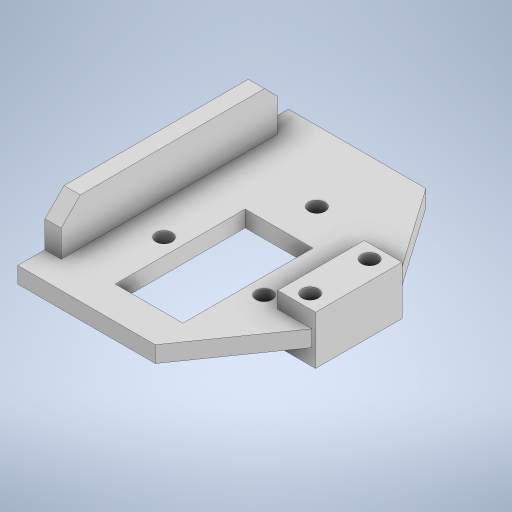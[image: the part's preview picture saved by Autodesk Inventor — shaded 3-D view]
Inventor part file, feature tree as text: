
AUTODESK INVENTOR PART (.ipt)
format: ipt  version: 2023 (Build 270158000, 158)  size: 316,416 bytes
history: native  units: mm
features: extrude x4, sketch x4, other x1
ambient origin geometry x8: Origin, YZ Plane, XZ Plane, XY Plane, X Axis, Y Axis, Z Axis, Center Point
bodies: Body1 (feature_tree)
feature tree (9):
  other  "Sólido1"
  extrude  "Extrusión1"  TaperAngle=135.0deg  [1 undecoded]
  extrude  "Extrusión2"  Depth=40.0mm
  extrude  "Extrusión3"  Depth=3.0mm TaperAngle=0.0deg
  extrude  "Extrusión4"  Depth=38.0mm
  sketch  "Boceto1"  dims[d0=135.0deg d2=135.0deg]
  sketch  "Boceto2"  dims[d3=135.0deg d5=40.0mm]
  sketch  "Boceto3"  dims[d6=20.0mm d7=3.0mm d8=0.0mm]
  sketch  "Boceto4"  dims[d9=50.0mm d10=38.0mm d11=25.307274mm d12=25.307274mm d13=12.5mm d14=24.0mm d15=6.0mm d16=12.0mm d17=3.0mm d18=3.0mm d19=3.0mm d20=3.0mm d21=3.0mm d22=7.0mm d23=3.0mm d24=0.0mm d25=7.0mm d26=9.0mm d27=0.0mm d28=3.0mm d29=3.0mm d30=11.0mm d31=5.5mm d34=8.0mm d35=8.0mm d36=9.0mm d37=0.0mm]
note: 1 required parameter value undecoded (feature->parameter linkage not recoverable at this tier; creation-order binding heuristic only, values carry confidence <= 0.55)
